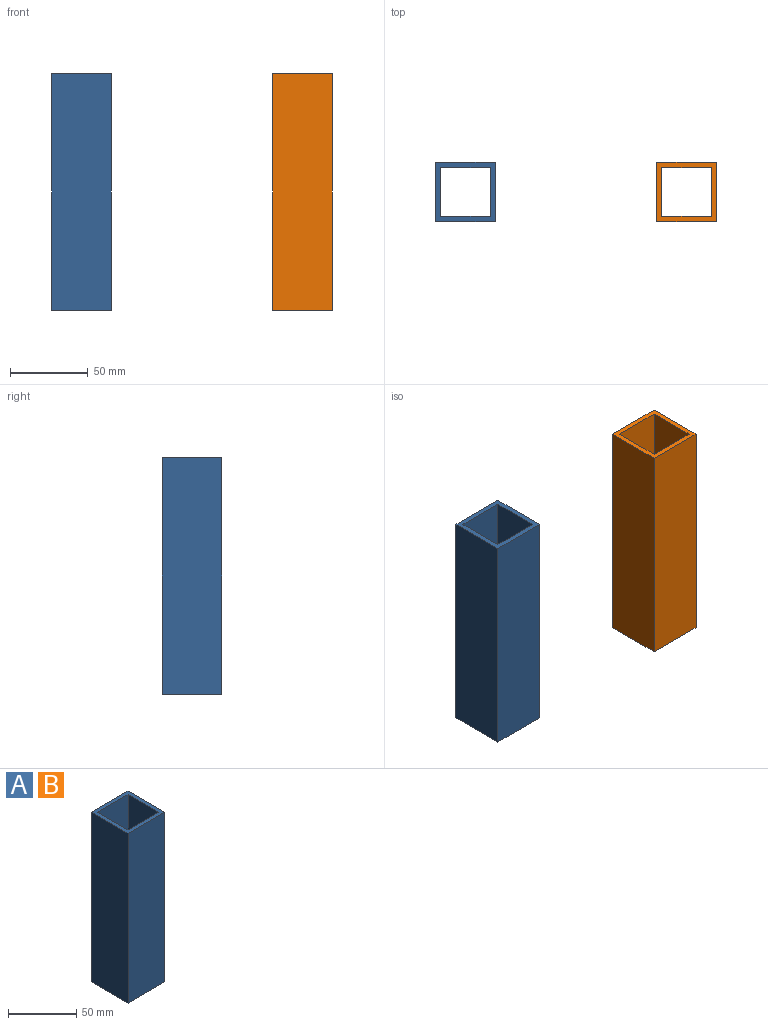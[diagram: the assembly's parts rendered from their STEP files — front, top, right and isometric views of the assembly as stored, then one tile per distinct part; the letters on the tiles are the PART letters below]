
ASSEMBLY  parts=2 mates=2
PART A: 10 faces, bbox 38.1x38.1x152.4 mm
  f0: plane 152.4x31.75mm, normal (1,0,0), area 4838.7mm2, adj f1,f7,f8,f9
  f1: plane 152.4x31.75mm, normal (0,-1,0), area 4838.7mm2, adj f0,f2,f8,f9
  f2: plane 152.4x31.75mm, normal (-1,0,0), area 4838.7mm2, adj f1,f7,f8,f9
  f3: plane 152.4x38.1mm, normal (-1,0,0), area 5806.4mm2, adj f4,f6,f8,f9
  f4: plane 152.4x38.1mm, normal (0,-1,0), area 5806.4mm2, adj f3,f5,f8,f9
  f5: plane 152.4x38.1mm, normal (1,0,0), area 5806.4mm2, adj f4,f6,f8,f9
  f6: plane 152.4x38.1mm, normal (0,1,0), area 5806.4mm2, adj f3,f5,f8,f9
  f7: plane 152.4x31.75mm, normal (0,1,0), area 4838.7mm2, adj f0,f2,f8,f9
  f8: plane 38.1x38.1mm, normal (0,0,1), area 443.5mm2, adj f0,f1,f2,f3,f4,f5,f6,f7
  f9: plane 38.1x38.1mm, normal (0,0,-1), area 443.5mm2, adj f0,f1,f2,f3,f4,f5,f6,f7
PART B: same geometry as A
PLACE A t=(-65.53,-3.39,-12.45)mm fixed
PLACE B rot(axis=(0,0,-1),90deg) t=(76.71,34.71,-12.45)mm
MATE planar A.f4 <-> B.f5  axis (0,-1,0) through (-46.48,-3.39,63.75)mm
MATE planar A.f8 <-> B.f8  axis (0,0,1) through (-46.48,15.66,139.95)mm
